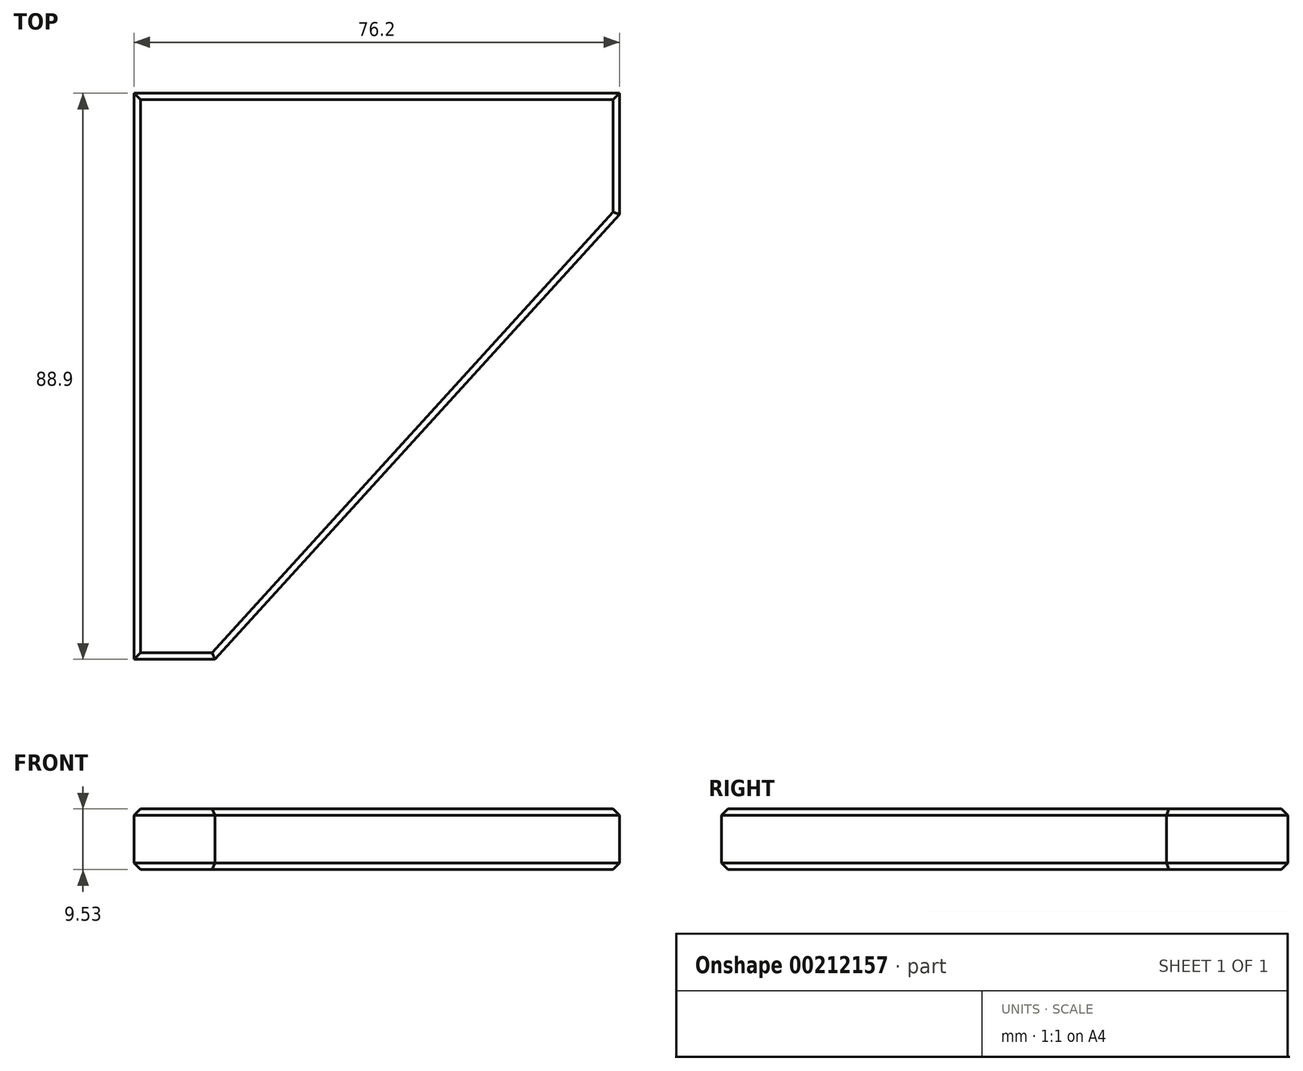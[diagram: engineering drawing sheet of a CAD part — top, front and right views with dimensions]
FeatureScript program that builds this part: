
annotation { "Feature Type Name" : "Feature", "Feature Type Description" : "" }
export const myFeature = defineFeature(function(context is Context, id is Id, definition is map)
    precondition{}
    {
        {
            var Q0;
            Q0=qCreatedBy(makeId("Top.planeOp"),FACE);
            var sketch = newSketch(context, id + "F0", { "sketchPlane" : qUnion([Q0])});
            skLineSegment(sketch, "E0", {"start": v(0, 0) * mm, "end": v(76.2, 0) * mm});
            skLineSegment(sketch, "E1", {"start": v(76.2, 0) * mm, "end": v(76.2, -19.05) * mm});
            skLineSegment(sketch, "E2", {"start": v(76.2, -19.05) * mm, "end": v(12.7, -88.9) * mm});
            skLineSegment(sketch, "E3", {"start": v(12.7, -88.9) * mm, "end": v(0, -88.9) * mm});
            skLineSegment(sketch, "E4", {"start": v(0, -88.9) * mm, "end": v(0, 0) * mm});
            skSolve(sketch);
        }
        {
            var Q0;
            Q0=makeQuery(id+"F0.imprint","IMPRINT",FACE,{"disambiguationData":[TD([[makeQuery(id+"F0.imprint","IMPRINT",EDGE,{"derivedFrom":sQuery(id+"F0.wireOp",EDGE,"E0")}),-1.0]])]});
            extrude(context, id + "F1", {"entities" : qUnion([Q0]), "depth" : 9.52 * mm});
        }
        {
            var Q0;
            Q0=makeQuery(id+"F1.opExtrude","CAP_FACE",FACE,{"disambiguationData":[OSD([sQuery(id+"F0.wireOp",EDGE,"E0"),sQuery(id+"F0.wireOp",EDGE,"E1"),sQuery(id+"F0.wireOp",EDGE,"E2"),sQuery(id+"F0.wireOp",EDGE,"E3"),sQuery(id+"F0.wireOp",EDGE,"E4")])],"isStart":false});
            var Q1;
            Q1=makeQuery(id+"F1.opExtrude","CAP_FACE",FACE,{"disambiguationData":[OSD([sQuery(id+"F0.wireOp",EDGE,"E0"),sQuery(id+"F0.wireOp",EDGE,"E1"),sQuery(id+"F0.wireOp",EDGE,"E2"),sQuery(id+"F0.wireOp",EDGE,"E3"),sQuery(id+"F0.wireOp",EDGE,"E4")])],"isStart":true});
            chamfer(context, id + "F2", {"entities" : qUnion([Q0, Q1]), "width" : 1.02 * mm, "tangentPropagation" : true});
        }
    });
